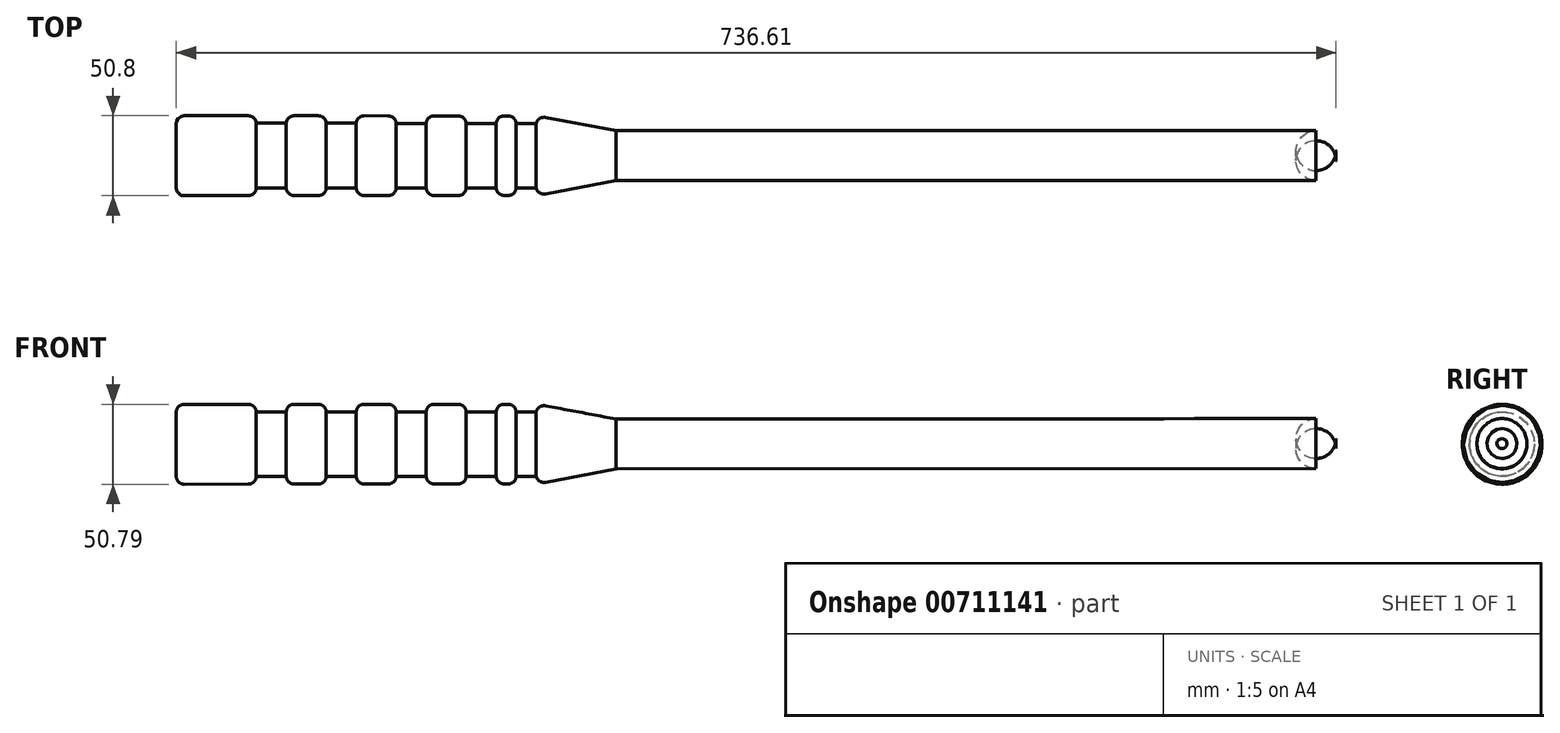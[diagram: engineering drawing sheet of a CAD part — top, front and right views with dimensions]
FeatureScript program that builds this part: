
annotation { "Feature Type Name" : "Feature", "Feature Type Description" : "" }
export const myFeature = defineFeature(function(context is Context, id is Id, definition is map)
    precondition{}
    {
        {
            var Q0;
            Q0=qCreatedBy(makeId("Front.planeOp"),FACE);
            var sketch = newSketch(context, id + "F0", { "sketchPlane" : qUnion([Q0])});
            skLineSegment(sketch, "E0.bottom", {"start": v(0, 0) * mm, "end": v(736.6, 0.4) * mm});
            skLineSegment(sketch, "E1", {"start": v(-0.01, 25.4) * mm, "end": v(0, 0) * mm});
            skLineSegment(sketch, "E2", {"start": v(736.57, 16.28) * mm, "end": v(736.6, 0.4) * mm});
            skLineSegment(sketch, "E3", {"start": v(736.57, 16.28) * mm, "end": v(279.4, 16.03) * mm});
            skLineSegment(sketch, "E4", {"start": v(228.59, 20.64) * mm, "end": v(228.59, 25.53) * mm});
            skLineSegment(sketch, "E5", {"start": v(279.4, 16.03) * mm, "end": v(279.38, 41.43) * mm, "construction": true});
            skLineSegment(sketch, "E6", {"start": v(228.59, 25.53) * mm, "end": v(279.4, 16.03) * mm});
            skLineSegment(sketch, "E7", {"start": v(-0.01, 25.4) * mm, "end": v(50.79, 25.4) * mm});
            skLineSegment(sketch, "E8", {"start": v(50.79, 25.4) * mm, "end": v(50.79, 20.64) * mm});
            skLineSegment(sketch, "E9", {"start": v(50.79, 20.64) * mm, "end": v(69.84, 20.64) * mm});
            skLineSegment(sketch, "E10", {"start": v(69.84, 20.64) * mm, "end": v(69.84, 25.4) * mm});
            skLineSegment(sketch, "E11", {"start": v(69.84, 25.4) * mm, "end": v(95.24, 25.4) * mm});
            skLineSegment(sketch, "E12", {"start": v(95.24, 25.4) * mm, "end": v(95.24, 20.64) * mm});
            skLineSegment(sketch, "E13", {"start": v(95.24, 20.64) * mm, "end": v(114.29, 20.64) * mm});
            skLineSegment(sketch, "E14", {"start": v(114.29, 20.64) * mm, "end": v(114.29, 25.4) * mm});
            skLineSegment(sketch, "E15", {"start": v(114.29, 25.4) * mm, "end": v(139.69, 25.4) * mm});
            skLineSegment(sketch, "E16", {"start": v(139.69, 25.4) * mm, "end": v(139.69, 20.64) * mm});
            skLineSegment(sketch, "E17", {"start": v(139.69, 20.64) * mm, "end": v(158.74, 20.64) * mm});
            skLineSegment(sketch, "E18", {"start": v(158.74, 20.64) * mm, "end": v(158.74, 25.4) * mm});
            skLineSegment(sketch, "E19", {"start": v(158.74, 25.4) * mm, "end": v(184.14, 25.4) * mm});
            skLineSegment(sketch, "E20", {"start": v(184.14, 25.4) * mm, "end": v(184.14, 20.64) * mm});
            skLineSegment(sketch, "E21", {"start": v(184.14, 20.64) * mm, "end": v(203.19, 20.64) * mm});
            skLineSegment(sketch, "E22", {"start": v(203.19, 20.64) * mm, "end": v(203.19, 25.4) * mm});
            skLineSegment(sketch, "E23", {"start": v(228.59, 20.64) * mm, "end": v(215.89, 20.63) * mm});
            skLineSegment(sketch, "E24", {"start": v(215.89, 20.63) * mm, "end": v(215.89, 25.4) * mm});
            skLineSegment(sketch, "E25", {"start": v(215.89, 25.4) * mm, "end": v(203.19, 25.4) * mm});
            skSolve(sketch);
        }
        {
            var Q0;
            Q0=makeQuery(id+"F0.imprint","IMPRINT",FACE,{"disambiguationData":[TD([[makeQuery(id+"F0.imprint","IMPRINT",EDGE,{"derivedFrom":sQuery(id+"F0.wireOp",EDGE,"E0.bottom")}),1.0]])]});
            var Q1;
            Q1=sQuery(id+"F0.wireOp",EDGE,"E0.bottom");
            revolve(context, id + "F1", {"surfaceOperationType" : NewSurfaceOperationType.NEW, "entities" : qUnion([Q0]), "axis" : qUnion([Q1]), "revolveType" : RevolveType.FULL});
        }
        {
            var Q0;
            Q0=makeQuery(id+"F1.opRevolve","SWEPT_EDGE",EDGE,{"disambiguationData":[OSD([sQuery(id+"F0.wireOp",EDGE,"5mtGLD47-Hyby-eXoI-qWzB-otnrppbMWody"),sQuery(id+"F0.wireOp",EDGE,"E2")])]});
            fillet(context, id + "F2", {"entities" : qUnion([Q0]), "radius" : 12.7 * mm, "tangentPropagation" : true, "allowEdgeOverflow" : false});
        }
        {
            var Q0;
            Q0=makeQuery(id+"F1.opRevolve","SWEPT_FACE",FACE,{"disambiguationData":[OSD([sQuery(id+"F0.wireOp",EDGE,"WKiRInXj-1ga8-rFoD-k9XS-gQYNPbhYGXvm")])]});
            var Q1;
            Q1=makeQuery(id+"F1.opRevolve","SWEPT_FACE",FACE,{"disambiguationData":[OSD([sQuery(id+"F0.wireOp",EDGE,"ih1xmPdh-AKYX-WoZ5-Cpn2-NlbMEW1btYl0")])]});
            var Q2;
            Q2=makeQuery(id+"F1.opRevolve","SWEPT_FACE",FACE,{"disambiguationData":[OSD([sQuery(id+"F0.wireOp",EDGE,"QTdn6awc-y5YB-GQqe-F7up-TDOusICONGy0")])]});
            var Q3;
            Q3=makeQuery(id+"F1.opRevolve","SWEPT_FACE",FACE,{"disambiguationData":[OSD([sQuery(id+"F0.wireOp",EDGE,"TIt7zwxh-FzPx-6VAx-3wsv-LmcWDP6k9hZc")])]});
            var Q4;
            Q4=makeQuery(id+"F1.opRevolve","SWEPT_FACE",FACE,{"disambiguationData":[OSD([sQuery(id+"F0.wireOp",EDGE,"RoDJkw7K-wBMt-Kahf-k8fk-i6e8TwBbIPca")])]});
            var Q5;
            Q5=makeQuery(id+"F1.opRevolve","SWEPT_FACE",FACE,{"disambiguationData":[OSD([sQuery(id+"F0.wireOp",EDGE,"E1")])]});
            fillet(context, id + "F3", {"entities" : qUnion([Q0, Q1, Q2, Q3, Q4, Q5]), "radius" : 5.08 * mm, "tangentPropagation" : true, "allowEdgeOverflow" : false});
        }
        {
            var Q0;
            Q0=makeQuery(id+"F1.opRevolve","SWEPT_EDGE",EDGE,{"disambiguationData":[OSD([sQuery(id+"F0.wireOp",EDGE,"E7"),sQuery(id+"F0.wireOp",EDGE,"E8")])]});
            var Q1;
            Q1=makeQuery(id+"F1.opRevolve","SWEPT_EDGE",EDGE,{"disambiguationData":[OSD([sQuery(id+"F0.wireOp",EDGE,"E10"),sQuery(id+"F0.wireOp",EDGE,"E11")])]});
            var Q2;
            Q2=makeQuery(id+"F1.opRevolve","SWEPT_EDGE",EDGE,{"disambiguationData":[OSD([sQuery(id+"F0.wireOp",EDGE,"E11"),sQuery(id+"F0.wireOp",EDGE,"E12")])]});
            var Q3;
            Q3=makeQuery(id+"F1.opRevolve","SWEPT_EDGE",EDGE,{"disambiguationData":[OSD([sQuery(id+"F0.wireOp",EDGE,"E15"),sQuery(id+"F0.wireOp",EDGE,"E16")])]});
            var Q4;
            Q4=makeQuery(id+"F1.opRevolve","SWEPT_EDGE",EDGE,{"disambiguationData":[OSD([sQuery(id+"F0.wireOp",EDGE,"E19"),sQuery(id+"F0.wireOp",EDGE,"E20")])]});
            var Q5;
            Q5=makeQuery(id+"F1.opRevolve","SWEPT_EDGE",EDGE,{"disambiguationData":[OSD([sQuery(id+"F0.wireOp",EDGE,"E24"),sQuery(id+"F0.wireOp",EDGE,"E25")])]});
            var Q6;
            Q6=makeQuery(id+"F1.opRevolve","SWEPT_EDGE",EDGE,{"disambiguationData":[OSD([sQuery(id+"F0.wireOp",EDGE,"E22"),sQuery(id+"F0.wireOp",EDGE,"E25")])]});
            var Q7;
            Q7=makeQuery(id+"F1.opRevolve","SWEPT_EDGE",EDGE,{"disambiguationData":[OSD([sQuery(id+"F0.wireOp",EDGE,"E18"),sQuery(id+"F0.wireOp",EDGE,"E19")])]});
            var Q8;
            Q8=makeQuery(id+"F1.opRevolve","SWEPT_EDGE",EDGE,{"disambiguationData":[OSD([sQuery(id+"F0.wireOp",EDGE,"E14"),sQuery(id+"F0.wireOp",EDGE,"E15")])]});
            fillet(context, id + "F4", {"entities" : qUnion([Q0, Q1, Q2, Q3, Q4, Q5, Q6, Q7, Q8]), "radius" : 5.08 * mm, "tangentPropagation" : true, "allowEdgeOverflow" : false});
        }
        {
            var Q0;
            Q0=makeQuery(id+"F1.opRevolve","SWEPT_EDGE",EDGE,{"disambiguationData":[OSD([sQuery(id+"F0.wireOp",EDGE,"E4"),sQuery(id+"F0.wireOp",EDGE,"E6")])]});
            fillet(context, id + "F5", {"entities" : qUnion([Q0]), "radius" : 5.08 * mm, "tangentPropagation" : true, "allowEdgeOverflow" : false});
        }
    });
